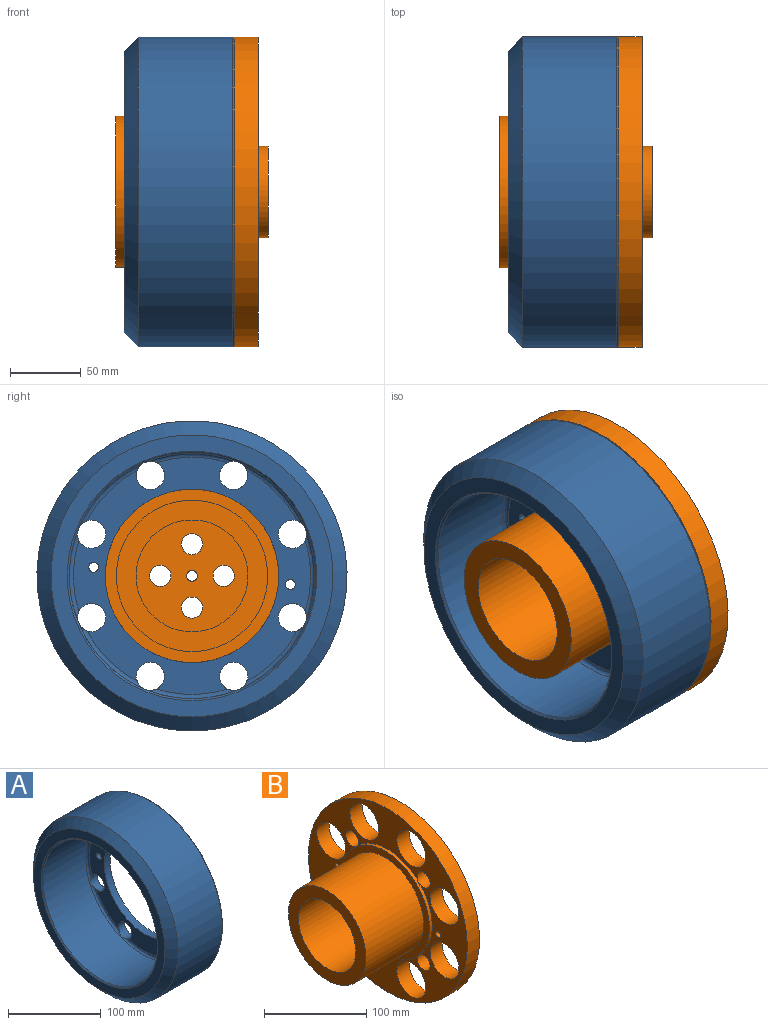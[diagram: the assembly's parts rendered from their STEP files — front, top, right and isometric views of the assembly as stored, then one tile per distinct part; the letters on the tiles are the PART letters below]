
ASSEMBLY  parts=2 mates=1
PART A: 27 faces, bbox 78x238.1x238.1 mm
  f0: torus R=84.1mm, axis (-1,0,0), area 279.4mm2, adj f10,f11,f23,f24
  f1: torus R=84.1mm, axis (-1,0,0), area 279.4mm2, adj f10,f11,f22,f23
  f2: torus R=84.1mm, axis (-1,0,0), area 279.6mm2, adj f10,f11,f19,f22
  f3: torus R=84.1mm, axis (-1,0,0), area 279.4mm2, adj f10,f11,f18,f21
  f4: torus R=84.1mm, axis (-1,0,0), area 279.4mm2, adj f10,f11,f17,f20
  f5: torus R=84.1mm, axis (-1,0,0), area 279.4mm2, adj f10,f11,f19,f21
  f6: torus R=84.1mm, axis (-1,0,0), area 279.4mm2, adj f10,f11,f18,f20
  f7: plane 218x218mm, normal (1,0,0), area 22852.7mm2, adj f13,f14,f17,f18,f19,f20,f21,f22
  f8: cylinder r=110mm len=220mm, axis (-1,0,0), area 46307.1mm2, adj f14,f15
  f9: plane 200x200mm, normal (-1,0,0), area 6810.2mm2, adj f15,f16
  f10: cylinder r=87.1mm len=174.2mm, axis (-1,0,0), area 35353.3mm2, adj f0,f1,f2,f3,f4,f5,f6,f12
  f11: plane 168.2x168.2mm, normal (-1,0,0), area 7996.1mm2, adj f0,f1,f2,f3,f4,f5,f6,f12
  f12: torus R=84.1mm, axis (-1,0,0), area 279.4mm2, adj f10,f11,f17,f24
  f13: cylinder r=61.5mm len=123mm, axis (1,0,0), area 3477.7mm2, adj f7,f11
  f14: torus R=109mm, axis (1,0,0), area 1082.1mm2, adj f7,f8
  f15: cone r=100mm half-angle=45deg, axis (1,0,0), area 9330.1mm2, adj f8,f9
  f16: cone r=87.1mm half-angle=45deg, axis (-1,0,0), area 1092.2mm2, adj f9,f10
  f17: cylinder r=10mm len=20mm, axis (1,0,0), area 584.9mm2, adj f4,f7,f11,f12
  f18: cylinder r=10mm len=20mm, axis (1,0,0), area 584.9mm2, adj f3,f6,f7,f11
  f19: cylinder r=10mm len=20mm, axis (1,0,0), area 585mm2, adj f2,f5,f7,f11
  f20: cylinder r=10mm len=20mm, axis (1,0,0), area 584.9mm2, adj f4,f6,f7,f11
  f21: cylinder r=10mm len=20mm, axis (1,0,0), area 584.9mm2, adj f3,f5,f7,f11
  f22: cylinder r=10mm len=20mm, axis (1,0,0), area 585mm2, adj f1,f2,f7,f11
  f23: cylinder r=10mm len=20mm, axis (1,0,0), area 584.9mm2, adj f0,f1,f7,f11
  f24: cylinder r=10mm len=20mm, axis (1,0,0), area 584.9mm2, adj f0,f7,f11,f12
  f25: cylinder r=3.5mm len=9mm, axis (1,0,0), area 197.9mm2, adj f7,f11
  f26: cylinder r=3.5mm len=9mm, axis (1,0,0), area 197.9mm2, adj f7,f11
PART B: 34 faces, bbox 108x220x220 mm
  f0: plane 79.37x79.37mm, normal (-1,0,0), area 4194.2mm2, adj f10,f29,f30,f31,f32,f33
  f1: plane 65x65mm, normal (1,0,0), area 2565.3mm2, adj f2,f29,f30,f31,f32,f33
  f2: cylinder r=32.5mm len=65mm, axis (1,0,0), area 1429.4mm2, adj f1,f3
  f3: plane 220x220mm, normal (1,0,0), area 23547mm2, adj f2,f4,f11,f13,f15,f17,f19,f20
  f4: cylinder r=110mm len=220mm, axis (1,0,0), area 11749.6mm2, adj f3,f5
  f5: plane 220x220mm, normal (-1,0,0), area 14990.5mm2, adj f4,f6,f11,f13,f15,f17,f19,f20
  f6: cylinder r=61.5mm len=123mm, axis (1,0,0), area 1523.5mm2, adj f5,f7,f11,f12,f13,f14,f15,f16
  f7: plane 123x123mm, normal (-1,0,0), area 2828.7mm2, adj f6,f8
  f8: cylinder r=53.68mm len=107.37mm, axis (1,0,0), area 26983.9mm2, adj f7,f9
  f9: plane 107.37x107.37mm, normal (-1,0,0), area 4106.4mm2, adj f8,f10
  f10: cylinder r=39.68mm len=84mm, axis (1,0,0), area 20944.1mm2, adj f0,f9
  f11: cylinder r=9mm len=18mm, axis (1,0,0), area 967mm2, adj f3,f5,f6,f12
  f12: plane 3.92x3.92mm, normal (1,0,0), area 1.9mm2, adj f6,f11
  f13: cylinder r=9mm len=18mm, axis (1,0,0), area 967mm2, adj f3,f5,f6,f14
  f14: plane 3.92x3.92mm, normal (1,0,0), area 1.9mm2, adj f6,f13
  f15: cylinder r=9mm len=18mm, axis (1,0,0), area 967mm2, adj f3,f5,f6,f16
  f16: plane 3.92x3.92mm, normal (1,0,0), area 1.9mm2, adj f6,f15
  f17: cylinder r=9mm len=18mm, axis (1,0,0), area 967mm2, adj f3,f5,f6,f18
  f18: plane 3.92x3.92mm, normal (1,0,0), area 1.9mm2, adj f6,f17
  f19: cylinder r=3.5mm len=17mm, axis (1,0,0), area 373.8mm2, adj f3,f5
  f20: cylinder r=20mm len=40mm, axis (1,0,0), area 2136.3mm2, adj f3,f5
  f21: cylinder r=20mm len=40mm, axis (1,0,0), area 2136.3mm2, adj f3,f5
  f22: cylinder r=20mm len=40mm, axis (1,0,0), area 2136.3mm2, adj f3,f5
  f23: cylinder r=3.5mm len=17mm, axis (1,0,0), area 373.8mm2, adj f3,f5
  f24: cylinder r=20mm len=40mm, axis (1,0,0), area 2136.3mm2, adj f3,f5
  f25: cylinder r=20mm len=40mm, axis (1,0,0), area 2136.3mm2, adj f3,f5
  f26: cylinder r=20mm len=40mm, axis (1,0,0), area 2136.3mm2, adj f3,f5
  f27: cylinder r=20mm len=40mm, axis (1,0,0), area 2136.3mm2, adj f3,f5
  f28: cylinder r=20mm len=40mm, axis (1,0,0), area 2136.3mm2, adj f3,f5
  f29: cylinder r=3.83mm len=24mm, axis (1,0,0), area 577.8mm2, adj f0,f1
  f30: cylinder r=7.5mm len=24mm, axis (1,0,0), area 1131mm2, adj f0,f1
  f31: cylinder r=7.5mm len=24mm, axis (1,0,0), area 1131mm2, adj f0,f1
  f32: cylinder r=7.5mm len=24mm, axis (1,0,0), area 1131mm2, adj f0,f1
  f33: cylinder r=7.5mm len=24mm, axis (1,0,0), area 1131mm2, adj f0,f1
PLACE A t=(-31.38,-74.27,-39.17)mm
PLACE B t=(-9.36,-184.27,-39.17)mm
MATE parallel B.f29 <-> A.f13  axis (-1,0,0) through (-31.38,-184.27,-39.17)mm
